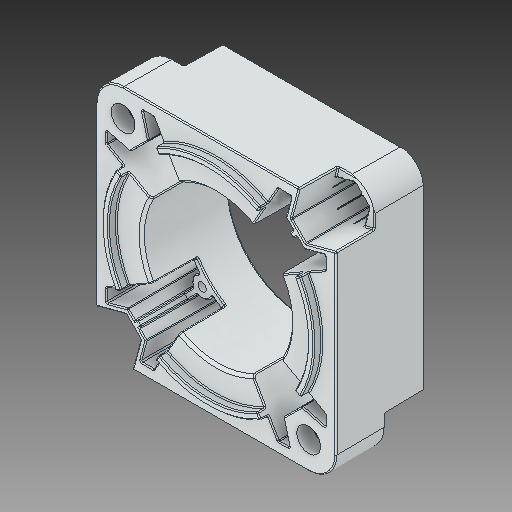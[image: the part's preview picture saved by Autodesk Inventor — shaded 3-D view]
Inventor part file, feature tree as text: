
AUTODESK INVENTOR PART (.ipt)
format: ipt  version: 2018 (Build 220112000, 112)  size: 1,586,176 bytes
history: native  units: in
note: dims shown in document units (in); Inventor stores cm internally (conversion verified against a paired STEP export)
features: chamfer x1
ambient origin geometry x8: Origin, YZ Plane, XZ Plane, XY Plane, X Axis, Y Axis, Z Axis, Center Point
bodies: Solid1 (feature_tree)
feature tree (1):
  chamfer  "Chamfer2"  [1 undecoded]
note: 1 required parameter value undecoded (feature->parameter linkage not recoverable at this tier; creation-order binding heuristic only, values carry confidence <= 0.55)
